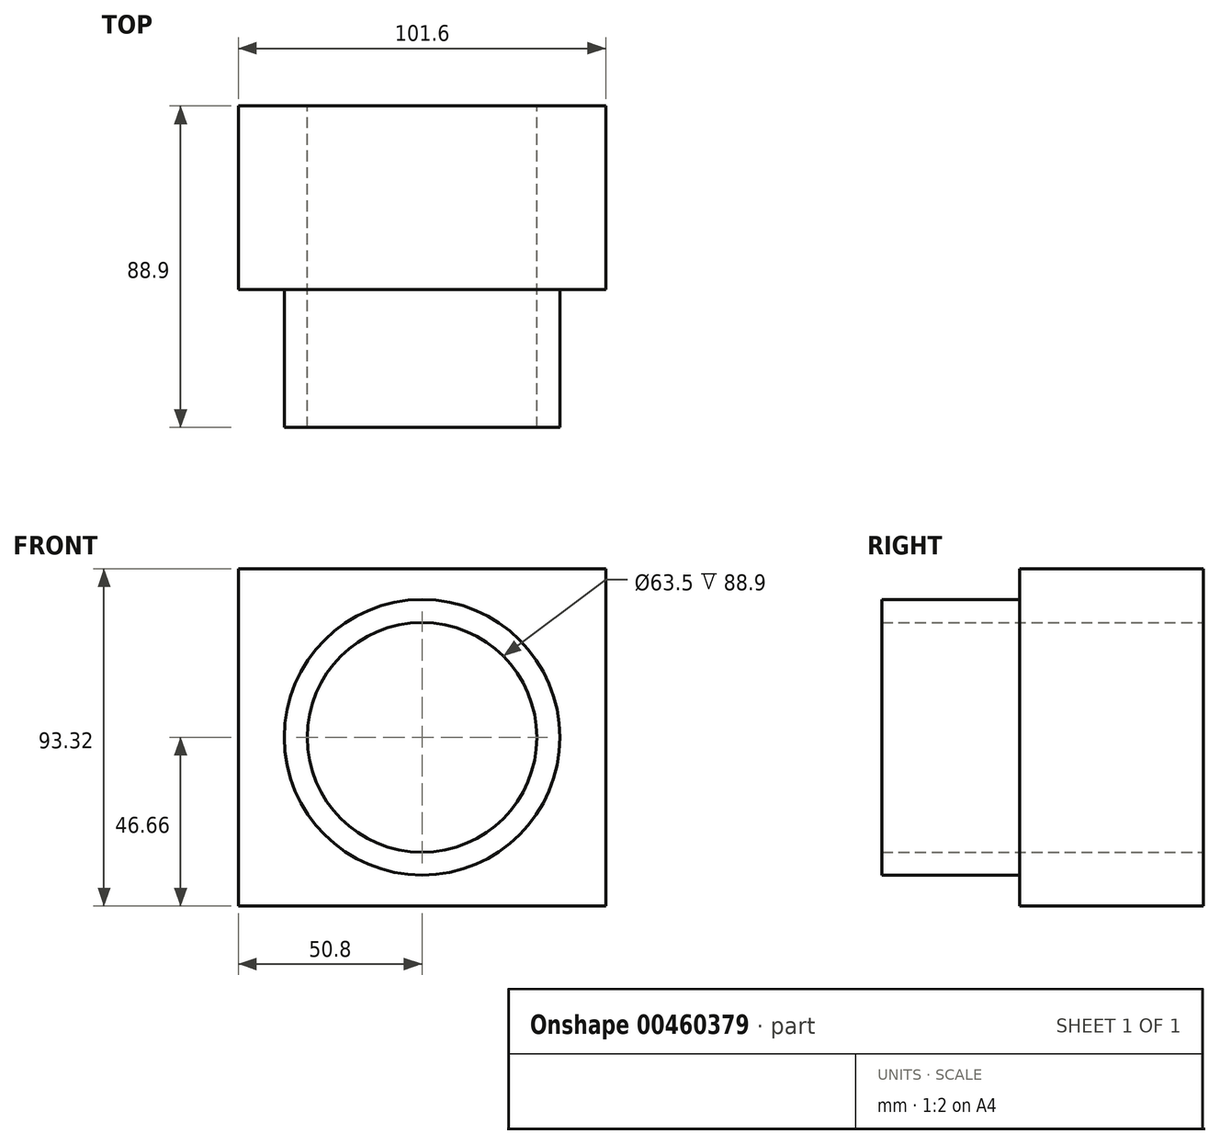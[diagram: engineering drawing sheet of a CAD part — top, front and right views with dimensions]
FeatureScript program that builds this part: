
annotation { "Feature Type Name" : "Feature", "Feature Type Description" : "" }
export const myFeature = defineFeature(function(context is Context, id is Id, definition is map)
    precondition{}
    {
        {
            var Q0;
            Q0=qCreatedBy(makeId("Front.planeOp"),FACE);
            var sketch = newSketch(context, id + "F0", { "sketchPlane" : qUnion([Q0])});
            skLineSegment(sketch, "E0.bottom", {"start": v(-50.8, 46.66) * mm, "end": v(50.8, 46.66) * mm});
            skLineSegment(sketch, "E0.top", {"start": v(-50.8, -46.66) * mm, "end": v(50.8, -46.66) * mm});
            skLineSegment(sketch, "E0.left", {"start": v(-50.8, 46.66) * mm, "end": v(-50.8, -46.66) * mm});
            skLineSegment(sketch, "E0.right", {"start": v(50.8, 46.66) * mm, "end": v(50.8, -46.66) * mm});
            skLineSegment(sketch, "E1", {"start": v(0, 94.97) * mm, "end": v(0, -130.45) * mm, "construction": true});
            skLineSegment(sketch, "E2", {"start": v(-113.3, 0) * mm, "end": v(130.07, 0) * mm, "construction": true});
            skSolve(sketch);
        }
        {
            var Q0;
            Q0 = qSketchRegion(id + "F0", true);
            extrude(context, id + "F1", {"entities" : qUnion([Q0]), "depth" : 50.8 * mm});
        }
        {
            var Q0;
            Q0=makeQuery(id+"F1.opExtrude","CAP_FACE",FACE,{"disambiguationData":[OSD([sQuery(id+"F0.wireOp",EDGE,"E0.bottom"),sQuery(id+"F0.wireOp",EDGE,"E0.top"),sQuery(id+"F0.wireOp",EDGE,"E0.left"),sQuery(id+"F0.wireOp",EDGE,"E0.right")])],"isStart":false});
            var sketch = newSketch(context, id + "F2", { "sketchPlane" : qUnion([Q0])});
            skCircle(sketch, "E3", {"center": v(0, 0) * mm, "radius": 38.1 * mm});
            skCircle(sketch, "E4", {"center": v(0, 0) * mm, "radius": 31.75 * mm});
            skSolve(sketch);
        }
        {
            var Q0;
            Q0 = qSketchRegion(id + "F2", true);
            extrude(context, id + "F3", {"entities" : qUnion([Q0]), "operationType" : NewBodyOperationType.ADD, "depth" : 38.1 * mm});
        }
        {
            var Q0;
            Q0=makeQuery(id+"F3.boolean.opBoolean","SPLIT",FACE,{"disambiguationData":[TD([makeQuery(id+"F3.opExtrude","SWEPT_FACE",FACE,{"disambiguationData":[OSD([sQuery(id+"F2.wireOp",EDGE,"E4")])]})])],"derivedFrom":makeQuery(id+"F1.opExtrude","CAP_FACE",FACE,{"disambiguationData":[OSD([sQuery(id+"F0.wireOp",EDGE,"E0.bottom"),sQuery(id+"F0.wireOp",EDGE,"E0.top"),sQuery(id+"F0.wireOp",EDGE,"E0.left"),sQuery(id+"F0.wireOp",EDGE,"E0.right")])],"isStart":false})});
            extrude(context, id + "F4", {"entities" : qUnion([Q0]), "operationType" : NewBodyOperationType.REMOVE, "oppositeDirection" : true, "depth" : 78.49 * mm});
        }
    });
